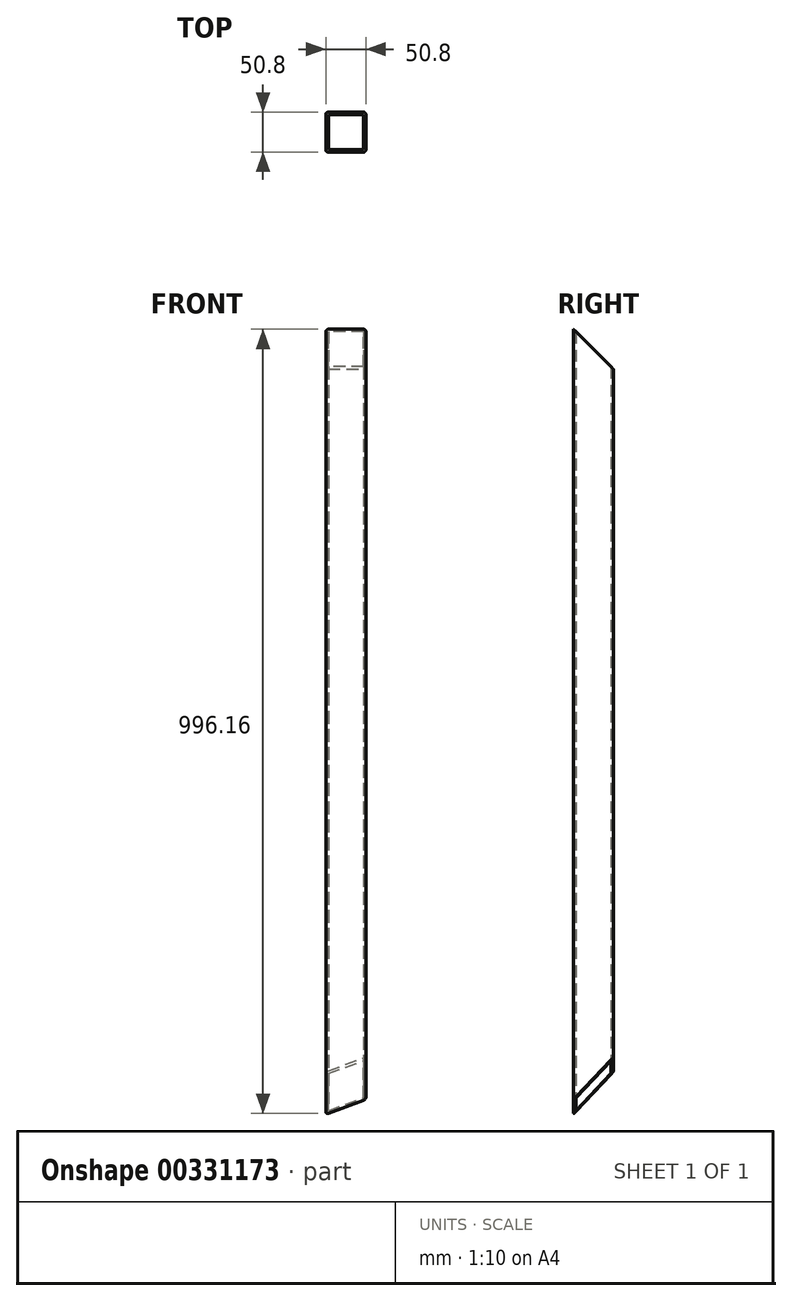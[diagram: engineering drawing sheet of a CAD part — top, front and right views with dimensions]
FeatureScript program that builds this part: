
annotation { "Feature Type Name" : "Feature", "Feature Type Description" : "" }
export const myFeature = defineFeature(function(context is Context, id is Id, definition is map)
    precondition{}
    {
        {
            var Q0;
            Q0=qCreatedBy(makeId("Top.planeOp"),FACE);
            var sketch = newSketch(context, id + "F0", { "sketchPlane" : qUnion([Q0])});
            skLineSegment(sketch, "E0.bottom", {"start": v(22.22, 25.4) * mm, "end": v(-22.22, 25.4) * mm});
            skLineSegment(sketch, "E0.top", {"start": v(22.22, -25.4) * mm, "end": v(-22.22, -25.4) * mm});
            skLineSegment(sketch, "E0.left", {"start": v(25.4, 22.22) * mm, "end": v(25.4, -22.22) * mm});
            skLineSegment(sketch, "E0.right", {"start": v(-25.4, 22.22) * mm, "end": v(-25.4, -22.22) * mm});
            skPoint(sketch, "E0.middle", {"position": v(0, 0) * mm});
            skPoint(sketch, "E1.visualSharp", {"position": v(-25.4, 25.4) * mm});
            skArc(sketch, "E1.filletArc", {"start": v(-22.22, 25.4) * mm, "mid": v(-24.47, 24.47) * mm, "end": v(-25.4, 22.22) * mm});
            skPoint(sketch, "E2.visualSharp", {"position": v(25.4, 25.4) * mm});
            skArc(sketch, "E2.filletArc", {"start": v(25.4, 22.22) * mm, "mid": v(24.47, 24.47) * mm, "end": v(22.22, 25.4) * mm});
            skPoint(sketch, "E3.visualSharp", {"position": v(-25.4, -25.4) * mm});
            skArc(sketch, "E3.filletArc", {"start": v(-25.4, -22.22) * mm, "mid": v(-24.47, -24.47) * mm, "end": v(-22.22, -25.4) * mm});
            skPoint(sketch, "E4.visualSharp", {"position": v(25.4, -25.4) * mm});
            skArc(sketch, "E4.filletArc", {"start": v(22.22, -25.4) * mm, "mid": v(24.47, -24.47) * mm, "end": v(25.4, -22.22) * mm});
            skLineSegment(sketch, "E5.0", {"start": v(22.23, 22.23) * mm, "end": v(-22.23, 22.23) * mm});
            skLineSegment(sketch, "E5.1", {"start": v(22.23, 22.23) * mm, "end": v(22.23, -22.22) * mm});
            skLineSegment(sketch, "E5.2", {"start": v(22.23, -22.22) * mm, "end": v(-22.22, -22.22) * mm});
            skLineSegment(sketch, "E5.3", {"start": v(-22.23, 22.23) * mm, "end": v(-22.22, -22.22) * mm});
            skSolve(sketch);
        }
        {
            var Q0;
            Q0 = qSketchRegion(id + "F0", true);
            extrude(context, id + "F1", {"entities" : qUnion([Q0]), "depth" : 1003.3 * mm});
        }
        {
            var Q0;
            Q0=makeQuery(id+"F1.opExtrude","SWEPT_FACE",FACE,{"disambiguationData":[OSD([sQuery(id+"F0.wireOp",EDGE,"E0.left")])]});
            var sketch = newSketch(context, id + "F2", { "sketchPlane" : qUnion([Q0])});
            skLineSegment(sketch, "E6.bottom", {"start": v(-25.4, 1003.3) * mm, "end": v(25.4, 1003.3) * mm});
            skLineSegment(sketch, "E6.left", {"start": v(25.4, 1003.3) * mm, "end": v(25.4, 952.5) * mm});
            skPoint(sketch, "E6.middle", {"position": v(0, 977.9) * mm});
            skLineSegment(sketch, "E7", {"start": v(25.4, 952.5) * mm, "end": v(-25.4, 1003.3) * mm});
            skPoint(sketch, "E6.top.end.orphan", {"position": v(-25.4, 952.5) * mm});
            skSolve(sketch);
        }
        {
            var Q0;
            Q0 = qSketchRegion(id + "F2", true);
            extrude(context, id + "F3", {"entities" : qUnion([Q0]), "operationType" : NewBodyOperationType.REMOVE, "endBound" : BoundingType.THROUGH_ALL, "oppositeDirection" : true, "depth" : 25.4 * mm});
        }
        {
            var Q0;
            Q0=makeQuery(id+"F1.opExtrude","SWEPT_FACE",FACE,{"disambiguationData":[OSD([sQuery(id+"F0.wireOp",EDGE,"E0.top")])]});
            var sketch = newSketch(context, id + "F4", { "sketchPlane" : qUnion([Q0])});
            skLineSegment(sketch, "E8.bottom", {"start": v(25.4, 0) * mm, "end": v(-25.4, 0) * mm});
            skLineSegment(sketch, "E8.left", {"start": v(25.4, 0) * mm, "end": v(25.4, 18.49) * mm});
            skPoint(sketch, "E8.middle", {"position": v(0, 9.24) * mm});
            skLineSegment(sketch, "E9", {"start": v(25.4, 18.49) * mm, "end": v(-25.4, 0) * mm});
            skPoint(sketch, "E8.right.end.orphan", {"position": v(-25.4, 18.49) * mm});
            skSolve(sketch);
        }
        {
            var Q0;
            Q0 = qSketchRegion(id + "F4", true);
            extrude(context, id + "F5", {"entities" : qUnion([Q0]), "operationType" : NewBodyOperationType.REMOVE, "endBound" : BoundingType.THROUGH_ALL, "oppositeDirection" : true, "depth" : 25.4 * mm});
        }
        {
            var Q0;
            Q0=makeQuery(id+"F5.boolean.opBoolean","INTERSECT",EDGE,{"derivedFrom":[makeQuery(id+"F1.opExtrude","SWEPT_FACE",FACE,{"disambiguationData":[OSD([sQuery(id+"F0.wireOp",EDGE,"E5.2")])]}),makeQuery(id+"F5.opExtrude","SWEPT_FACE",FACE,{"disambiguationData":[OSD([sQuery(id+"F4.wireOp",EDGE,"E9")])]})]});
            var Q1;
            Q1=makeQuery(id+"F5.boolean.opBoolean","INTERSECT",EDGE,{"derivedFrom":[makeQuery(id+"F1.opExtrude","SWEPT_FACE",FACE,{"disambiguationData":[OSD([sQuery(id+"F0.wireOp",EDGE,"E5.0")])]}),makeQuery(id+"F5.opExtrude","SWEPT_FACE",FACE,{"disambiguationData":[OSD([sQuery(id+"F4.wireOp",EDGE,"E9")])]})]});
            cPlane(context, id + "F6", {"entities" : qUnion([Q0, Q1]), "cplaneType" : CPlaneType.LINE_ANGLE, "offset" : 25.4 * mm, "angle" : 45 * degree, "oppositeDirection" : true, "width" : 152.4 * mm, "height" : 152.4 * mm});
        }
        {
            var Q0;
            Q0=qCreatedBy(id+"F6.planeOp",FACE);
            var sketch = newSketch(context, id + "F7", { "sketchPlane" : qUnion([Q0])});
            skLineSegment(sketch, "E10.bottom", {"start": v(-97.56, 88.02) * mm, "end": v(83.87, 88.02) * mm});
            skLineSegment(sketch, "E10.top", {"start": v(-97.56, -115.18) * mm, "end": v(83.87, -115.18) * mm});
            skLineSegment(sketch, "E10.left", {"start": v(-97.56, 88.02) * mm, "end": v(-97.56, -115.18) * mm});
            skLineSegment(sketch, "E10.right", {"start": v(83.87, 88.02) * mm, "end": v(83.87, -115.18) * mm});
            skPoint(sketch, "E10.middle", {"position": v(-6.85, -13.58) * mm});
            skSolve(sketch);
        }
        {
            var Q0;
            Q0 = qSketchRegion(id + "F7", true);
            extrude(context, id + "F8", {"entities" : qUnion([Q0]), "operationType" : NewBodyOperationType.REMOVE, "depth" : 50.8 * mm, "hasSecondDirection" : true, "secondDirectionOppositeDirection" : true, "secondDirectionDepth" : 6.35 * mm});
        }
    });
